# Revit family: Water_Refill_Station-Sensor_Operated-Murdock-H2O_To_Go-BF168_Series
name_source: partatom
category: Plumbing Fixtures
revit_build: Autodesk Revit 2018 (Build: 20170223_1515(x64)
units: mm (PartAtom-declared; Revit-internal decimal feet)

## family parameters
Cut with Voids When Loaded = No
Host = Face
OmniClass Number = 23.65.70.14.11
OmniClass Title = Drinking Fountains/Coolers
Part Type = Normal
Room Calculation Point = No
Round Connector Dimension = Use Radius
Shared = Yes

## types (2) — shared parameters
-LOGO Customer Specified Logo / Graphics = No
-WF1 1500-gallon capacity, NSF 42+53, 1 micron Lead Reduction Water Filter = No
-WF3 3000-gallon capacity, NSF 42+53, 1 micron Lead Reduction Water Filters = No
ADA Compliant = Yes
Activation By = Sensor (on Bottle Filler)
Assembly Code = D2010800
Bottle Filler Width = 8 1/8"
CW Connection = Yes
CWFU = 1.5
Cold Water Connection Diameter = 3/8"
Cold Water Connection Height = 30"
Cold Water Connection Radius = 3/16"
Cold Water Connection Width = 6 1/4"
Default Elevation = 0"
Description = H2O-To-Go!® Refrigerated, Sensor-Operated Water Refill Station
Fill Rate = 1.00 GPM
Finish = Stainless Steel-Murdock-Satin
Full Load Amps = 5 A
HW Connection = No
Height = 52 7/8"
IAPMO Compliance = AHRI Standard 1010, ANSI A117.1, NSF/ANSI 61, Section 9
Installation Type = Wall Mounted
Length = 23 3/4"
Manufacturer = Murdock
Material = Stainless Steel-Murdock-Satin
Maximum Run Time = 20 Seconds
Model = BF168
Mounting Height = 57 5/8"
Power = 120 VAC/9 VDC
Price = Prices may vary. Please consult Manufacturer Representative for most up-to-date price list.
Product Documentation Link = https://www.murdockmfg.com
Product Page URL = https://www.murdockmfg.com
Rated Watts = 390
Refrigerant Width = 10 7/8"
Shipping Weight = 48 lbs.
Type Comments = Hands-Free Operation
URL = https://www.murdockmfg.com
Vent Connection = No
WFU = 2
Warranty Information = Murdock Mfg.™ warrants that its products are free from defects in material or workmanship under normal use and service for a period of 18
months from date of shipment. The sealed refrigeration system is warranted for five years. Murdock’s liability under this warranty shall be discharged solely by replacement or repair of defective material, provided Murdock™ is notified in writing within one year from date of shipment, F.O.B. Industry, California
Warranty URL = https://www.murdockmfg.com
Waste Connection = Yes
Waste Connection Diameter = 1 1/4"
Waste Connection Height = 33"
Waste Connection Radius = 5/8"
Waste Connection Width = 3 1/2"
Water Deliver Rate = 8.0 GPH (30.3 LPH) of water at 50°F (10°C) cooled from 80°F (26.7°C) inlet water and 90°F (32.2°C) ambient
Width = 19"
cUPC Compliant = Yes
zero-valued in all types: HWFU

## per-type parameters (varying)
| type | -BCD Bottle Counter Display |
| BF168 | No |
| BF168-BCD | Yes |

## geometry (parser evidence)
native form markers: Sweep x3
no freeform markers — native parametric forms only
